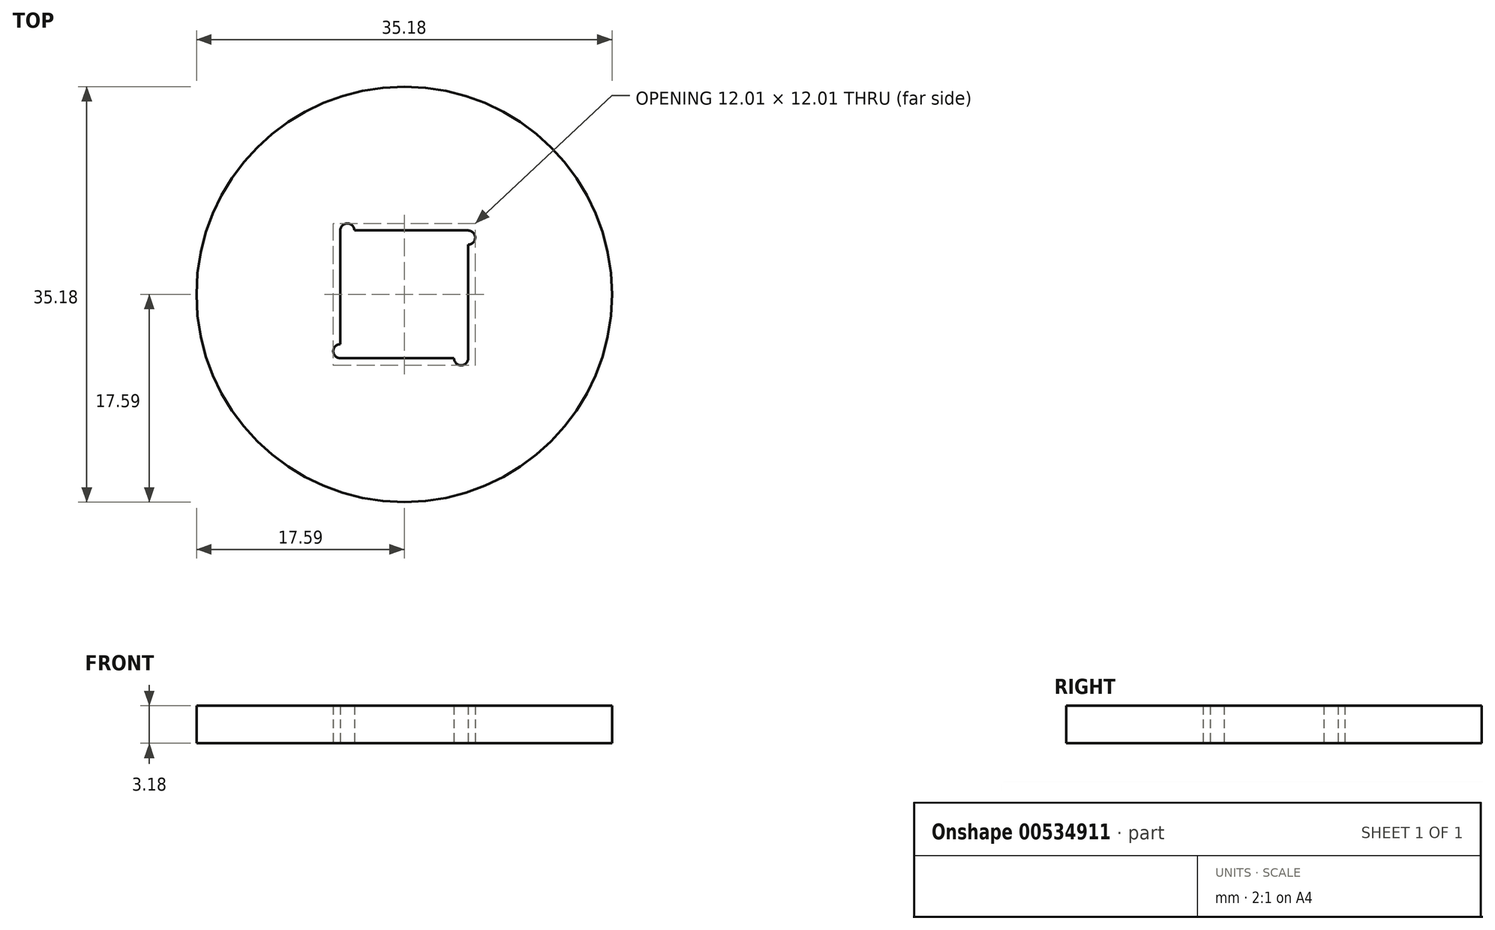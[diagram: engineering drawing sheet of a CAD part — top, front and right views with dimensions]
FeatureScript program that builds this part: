
annotation { "Feature Type Name" : "Feature", "Feature Type Description" : "" }
export const myFeature = defineFeature(function(context is Context, id is Id, definition is map)
    precondition{}
    {
        {
            var Q0;
            Q0=qCreatedBy(makeId("Top.planeOp"),FACE);
            var sketch = newSketch(context, id + "F0", { "sketchPlane" : qUnion([Q0])});
            skCircle(sketch, "E0", {"center": v(0, 0) * mm, "radius": 17.59 * mm});
            skLineSegment(sketch, "E1.top", {"start": v(5.41, 5.41) * mm, "end": v(-4.22, 5.41) * mm});
            skLineSegment(sketch, "E1.left", {"start": v(5.41, -5.41) * mm, "end": v(5.41, 4.22) * mm});
            skArc(sketch, "E2", {"start": v(4.22, -5.41) * mm, "mid": v(4.81, -6) * mm, "end": v(5.41, -5.41) * mm});
            skLineSegment(sketch, "E3.trimOffspring", {"start": v(4.22, -5.41) * mm, "end": v(-5.41, -5.41) * mm});
            skArc(sketch, "E4", {"start": v(-5.41, -4.22) * mm, "mid": v(-6, -4.81) * mm, "end": v(-5.41, -5.41) * mm});
            skLineSegment(sketch, "E5.trimOffspring", {"start": v(-5.41, -4.22) * mm, "end": v(-5.41, 5.41) * mm});
            skArc(sketch, "E6", {"start": v(-4.22, 5.41) * mm, "mid": v(-4.81, 6) * mm, "end": v(-5.41, 5.41) * mm});
            skArc(sketch, "E7", {"start": v(5.41, 4.22) * mm, "mid": v(6, 4.81) * mm, "end": v(5.41, 5.41) * mm});
            skSolve(sketch);
        }
        {
            var Q0;
            Q0 = qSketchRegion(id + "F0", true);
            extrude(context, id + "F1", {"entities" : qUnion([Q0]), "depth" : 3.17 * mm, "offsetDistance" : 25.4 * mm});
        }
    });
